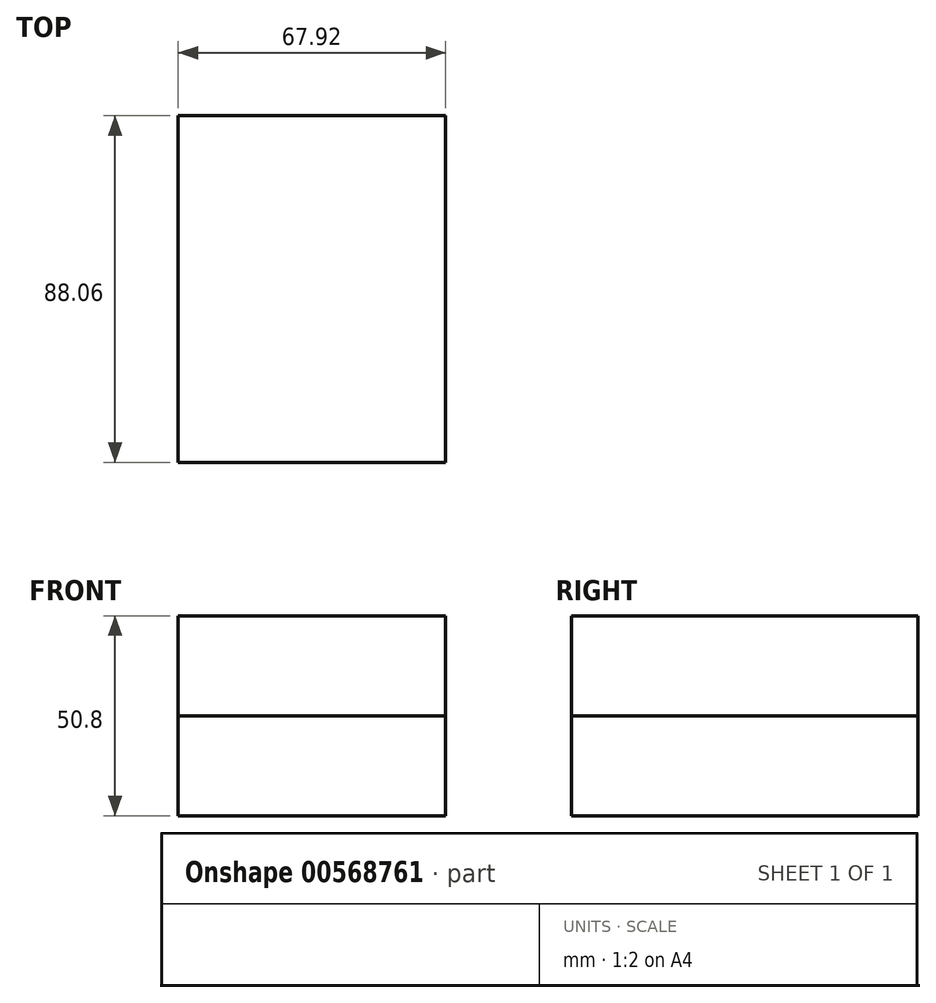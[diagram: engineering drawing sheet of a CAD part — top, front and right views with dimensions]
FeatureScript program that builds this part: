
annotation { "Feature Type Name" : "Feature", "Feature Type Description" : "" }
export const myFeature = defineFeature(function(context is Context, id is Id, definition is map)
    precondition{}
    {
        {
            var Q0;
            Q0=qCreatedBy(makeId("Top.planeOp"),FACE);
            var sketch = newSketch(context, id + "F0", { "sketchPlane" : qUnion([Q0])});
            skLineSegment(sketch, "E0.bottom", {"start": v(33.96, 44.03) * mm, "end": v(-33.96, 44.03) * mm});
            skLineSegment(sketch, "E0.top", {"start": v(33.96, -44.03) * mm, "end": v(-33.96, -44.03) * mm});
            skLineSegment(sketch, "E0.left", {"start": v(33.96, 44.03) * mm, "end": v(33.96, -44.03) * mm});
            skLineSegment(sketch, "E0.right", {"start": v(-33.96, 44.03) * mm, "end": v(-33.96, -44.03) * mm});
            skPoint(sketch, "E0.middle", {"position": v(0, 0) * mm});
            skSolve(sketch);
        }
        {
            var Q0;
            Q0=makeQuery(id+"F0.imprint","IMPRINT",FACE,{"disambiguationData":[TD([[makeQuery(id+"F0.imprint","IMPRINT",EDGE,{"derivedFrom":sQuery(id+"F0.wireOp",EDGE,"E0.bottom")}),1.0]])]});
            extrude(context, id + "F1", {"entities" : qUnion([Q0]), "depth" : 25.4 * mm, "offsetDistance" : 25.4 * mm});
        }
        {
            var Q0;
            Q0=makeQuery(id+"F1.opExtrude","CAP_FACE",FACE,{"disambiguationData":[OSD([sQuery(id+"F0.wireOp",EDGE,"E0.bottom"),sQuery(id+"F0.wireOp",EDGE,"E0.top"),sQuery(id+"F0.wireOp",EDGE,"E0.left"),sQuery(id+"F0.wireOp",EDGE,"E0.right")])],"isStart":false});
            extrude(context, id + "F2", {"entities" : qUnion([Q0]), "operationType" : NewBodyOperationType.ADD, "depth" : 25.4 * mm, "offsetDistance" : 25.4 * mm});
        }
        {
            var Q0;
            Q0=makeQuery(id+"F0.imprint","IMPRINT",FACE,{"disambiguationData":[TD([[makeQuery(id+"F0.imprint","IMPRINT",EDGE,{"derivedFrom":sQuery(id+"F0.wireOp",EDGE,"E0.bottom")}),1.0]])]});
            extrude(context, id + "F3", {"entities" : qUnion([Q0]), "depth" : 25.4 * mm});
        }
    });
